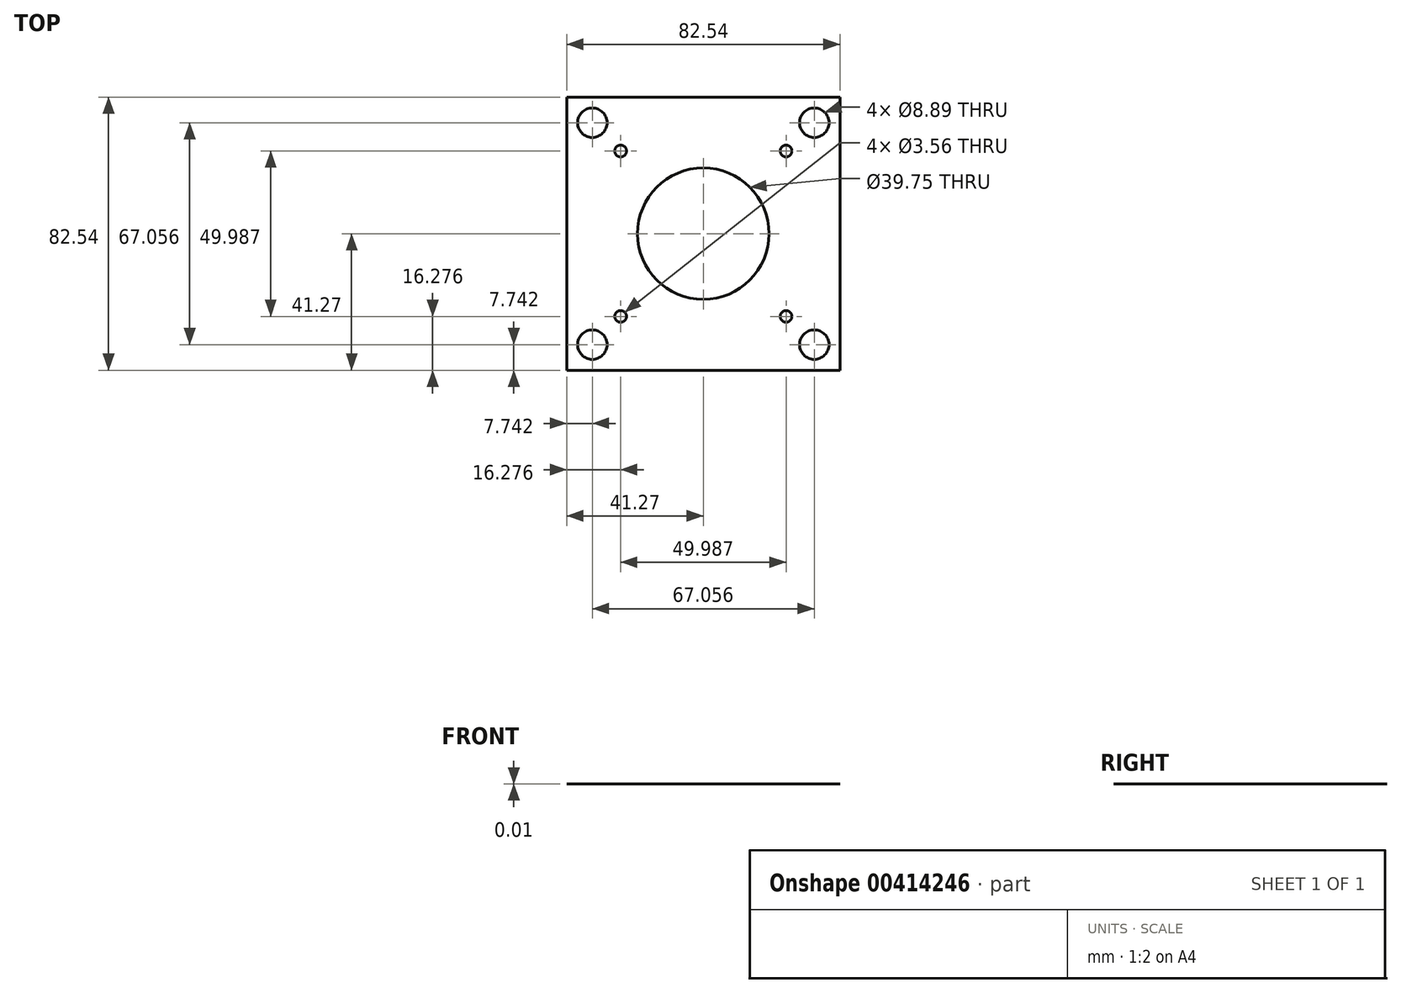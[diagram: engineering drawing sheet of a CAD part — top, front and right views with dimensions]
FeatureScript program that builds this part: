
annotation { "Feature Type Name" : "Feature", "Feature Type Description" : "" }
export const myFeature = defineFeature(function(context is Context, id is Id, definition is map)
    precondition{}
    {
        {
            var Q0;
            Q0=qCreatedBy(makeId("Top.planeOp"),FACE);
            var sketch = newSketch(context, id + "F0", { "sketchPlane" : qUnion([Q0])});
            skLineSegment(sketch, "E0.bottom", {"start": v(41.28, 41.27) * mm, "end": v(-41.28, 41.28) * mm});
            skLineSegment(sketch, "E0.top", {"start": v(41.28, -41.28) * mm, "end": v(-41.28, -41.28) * mm});
            skLineSegment(sketch, "E0.left", {"start": v(41.28, 41.28) * mm, "end": v(41.28, -41.28) * mm});
            skLineSegment(sketch, "E0.right", {"start": v(-41.28, 41.28) * mm, "end": v(-41.28, -41.28) * mm});
            skCircle(sketch, "E1", {"center": v(0, 0) * mm, "radius": 19.88 * mm});
            skLineSegment(sketch, "E2", {"start": v(0, 0) * mm, "end": v(0, 25) * mm, "construction": true});
            skLineSegment(sketch, "E3", {"start": v(0, 25) * mm, "end": v(25, 25) * mm, "construction": true});
            skCircle(sketch, "E4", {"center": v(25, 25) * mm, "radius": 1.78 * mm});
            skCircle(sketch, "E5.1.0", {"center": v(-25, 25) * mm, "radius": 1.78 * mm});
            skCircle(sketch, "E5.2.0", {"center": v(-25, -25) * mm, "radius": 1.78 * mm});
            skCircle(sketch, "E5.3.0", {"center": v(25, -25) * mm, "radius": 1.78 * mm});
            skLineSegment(sketch, "E6", {"start": v(0, 0) * mm, "end": v(41.28, 41.28) * mm, "construction": true});
            skCircle(sketch, "E7", {"center": v(33.53, 33.53) * mm, "radius": 4.45 * mm});
            skCircle(sketch, "E8.1.0", {"center": v(-33.53, 33.53) * mm, "radius": 4.45 * mm});
            skCircle(sketch, "E8.2.0", {"center": v(-33.53, -33.53) * mm, "radius": 4.45 * mm});
            skCircle(sketch, "E8.3.0", {"center": v(33.53, -33.53) * mm, "radius": 4.45 * mm});
            skLineSegment(sketch, "E9", {"start": v(0, 0) * mm, "end": v(41.28, 0) * mm, "construction": true});
            skSolve(sketch);
        }
        {
            var Q0;
            Q0=makeQuery(id+"F0.imprint","IMPRINT",FACE,{"disambiguationData":[TD([[makeQuery(id+"F0.imprint","IMPRINT",EDGE,{"derivedFrom":sQuery(id+"F0.wireOp",EDGE,"E0.bottom")}),1.0]])]});
            extrude(context, id + "F1", {"entities" : qUnion([Q0]), "depth" : 1 / 101.6 * mm});
        }
    });
